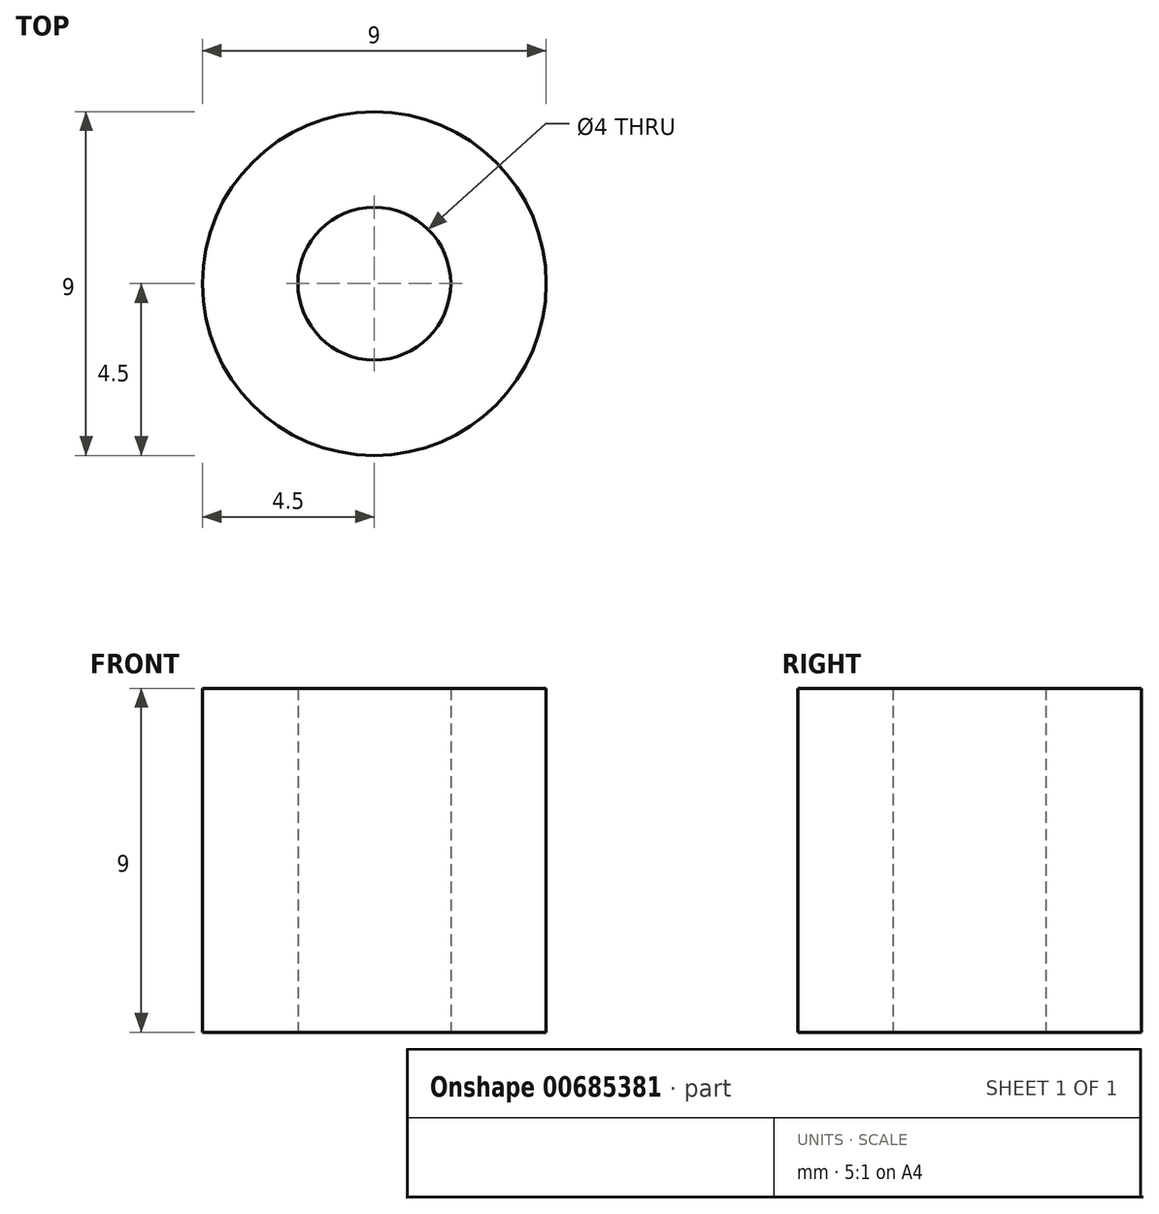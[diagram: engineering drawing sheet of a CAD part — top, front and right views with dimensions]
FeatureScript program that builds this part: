
annotation { "Feature Type Name" : "Feature", "Feature Type Description" : "" }
export const myFeature = defineFeature(function(context is Context, id is Id, definition is map)
    precondition{}
    {
        {
            var Q0;
            Q0=qCreatedBy(makeId("Top.planeOp"),FACE);
            var sketch = newSketch(context, id + "F0", { "sketchPlane" : qUnion([Q0])});
            skCircle(sketch, "E0", {"center": v(0, 0) * mm, "radius": 4.5 * mm});
            skCircle(sketch, "E1", {"center": v(0, 0) * mm, "radius": 2 * mm});
            skSolve(sketch);
        }
        {
            var Q0;
            Q0 = qSketchRegion(id + "F0", true);
            extrude(context, id + "F1", {"entities" : qUnion([Q0]), "depth" : 9 * mm, "offsetDistance" : 25 * mm});
        }
    });
